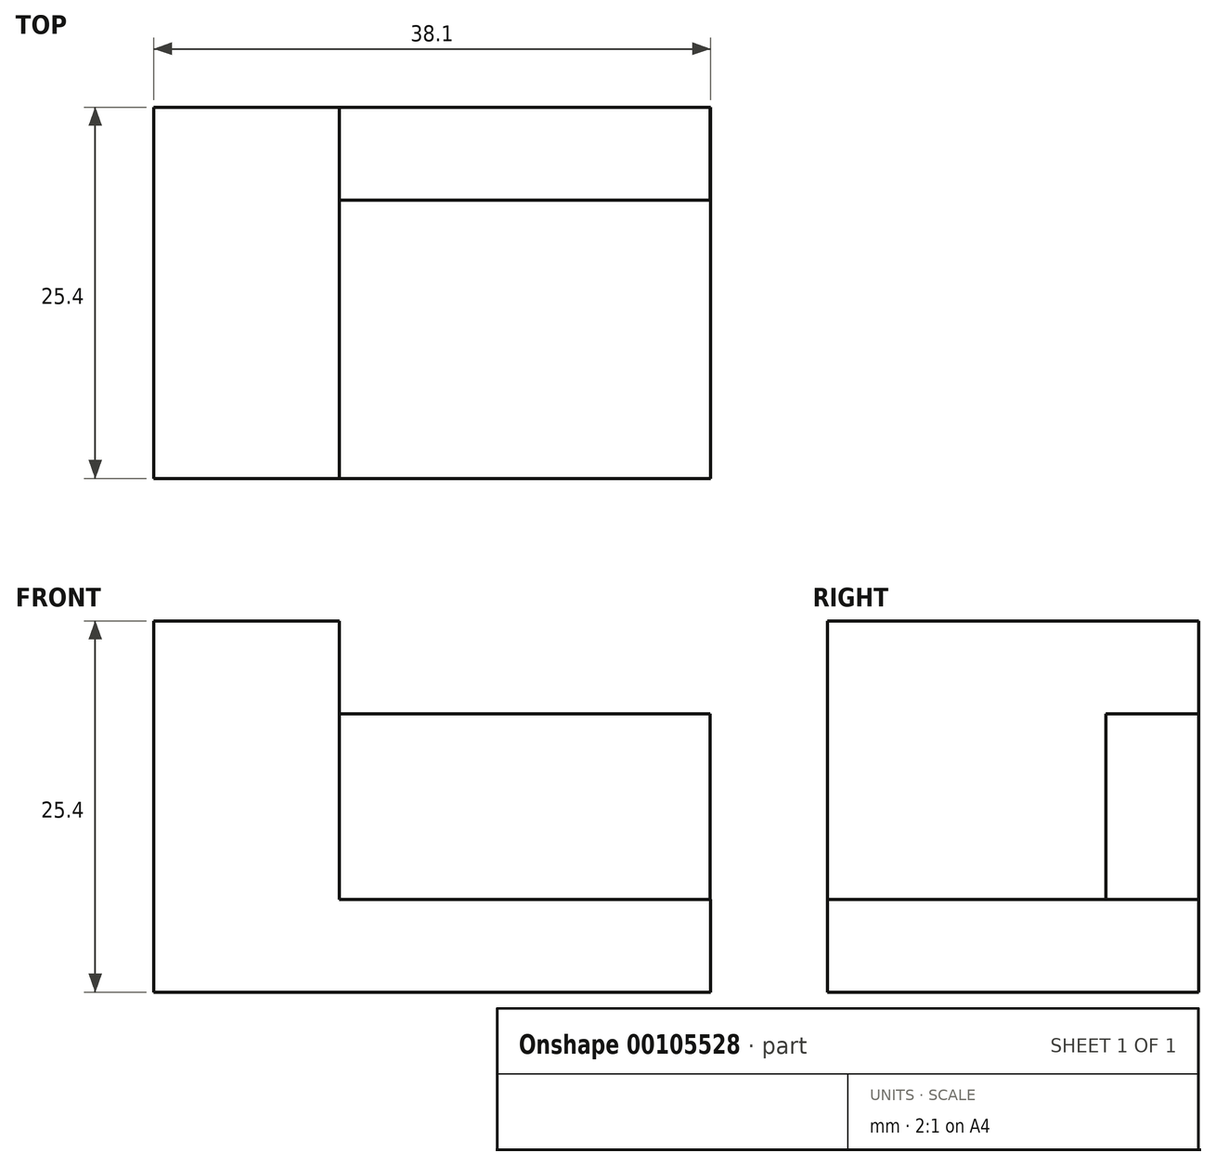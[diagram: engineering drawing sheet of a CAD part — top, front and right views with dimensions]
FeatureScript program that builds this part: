
annotation { "Feature Type Name" : "Feature", "Feature Type Description" : "" }
export const myFeature = defineFeature(function(context is Context, id is Id, definition is map)
    precondition{}
    {
        {
            var Q0;
            Q0=qCreatedBy(makeId("Front.planeOp"),FACE);
            var sketch = newSketch(context, id + "F0", { "sketchPlane" : qUnion([Q0])});
            skLineSegment(sketch, "E0", {"start": v(0, 0) * mm, "end": v(0, 19.05) * mm});
            skLineSegment(sketch, "E1", {"start": v(0, 19.05) * mm, "end": v(38.05, 19.05) * mm});
            skLineSegment(sketch, "E2", {"start": v(38.05, 19.05) * mm, "end": v(38.05, 0) * mm});
            skLineSegment(sketch, "E3", {"start": v(38.05, 0) * mm, "end": v(0, 0) * mm});
            skSolve(sketch);
        }
        {
            var Q0;
            Q0=makeQuery(id+"F0.imprint","IMPRINT",FACE,{"disambiguationData":[TD([[makeQuery(id+"F0.imprint","IMPRINT",EDGE,{"derivedFrom":sQuery(id+"F0.wireOp",EDGE,"E0")}),-1.0]])]});
            extrude(context, id + "F1", {"entities" : qUnion([Q0]), "depth" : 6.35 * mm});
        }
        {
            var Q0;
            Q0=qCreatedBy(makeId("Right.planeOp"),FACE);
            var sketch = newSketch(context, id + "F2", { "sketchPlane" : qUnion([Q0])});
            skLineSegment(sketch, "E4", {"start": v(0, 0) * mm, "end": v(0, 6.35) * mm});
            skLineSegment(sketch, "E5", {"start": v(0, 6.35) * mm, "end": v(-25.4, 6.35) * mm});
            skLineSegment(sketch, "E6", {"start": v(-25.4, 6.35) * mm, "end": v(-25.4, 0) * mm});
            skLineSegment(sketch, "E7", {"start": v(-25.4, 0) * mm, "end": v(0, 0) * mm});
            skSolve(sketch);
        }
        {
            var Q0;
            Q0=makeQuery(id+"F2.imprint","IMPRINT",FACE,{"disambiguationData":[TD([[makeQuery(id+"F2.imprint","IMPRINT",EDGE,{"derivedFrom":sQuery(id+"F2.wireOp",EDGE,"E4")}),1.0]])]});
            extrude(context, id + "F3", {"entities" : qUnion([Q0]), "operationType" : NewBodyOperationType.ADD, "depth" : 38.1 * mm});
        }
        {
            var Q0;
            Q0=qCreatedBy(makeId("Right.planeOp"),FACE);
            var sketch = newSketch(context, id + "F4", { "sketchPlane" : qUnion([Q0])});
            skLineSegment(sketch, "E8", {"start": v(0, 0) * mm, "end": v(0, 25.4) * mm});
            skLineSegment(sketch, "E9", {"start": v(0, 25.4) * mm, "end": v(-25.4, 25.4) * mm});
            skLineSegment(sketch, "E10", {"start": v(-25.4, 25.4) * mm, "end": v(-25.4, 0) * mm});
            skLineSegment(sketch, "E11", {"start": v(-25.4, 0) * mm, "end": v(0, 0) * mm});
            skSolve(sketch);
        }
        {
            var Q0;
            Q0=makeQuery(id+"F4.imprint","IMPRINT",FACE,{"disambiguationData":[TD([[makeQuery(id+"F4.imprint","IMPRINT",EDGE,{"derivedFrom":sQuery(id+"F4.wireOp",EDGE,"E8")}),1.0]])]});
            extrude(context, id + "F5", {"entities" : qUnion([Q0]), "operationType" : NewBodyOperationType.ADD, "depth" : 12.7 * mm});
        }
    });
